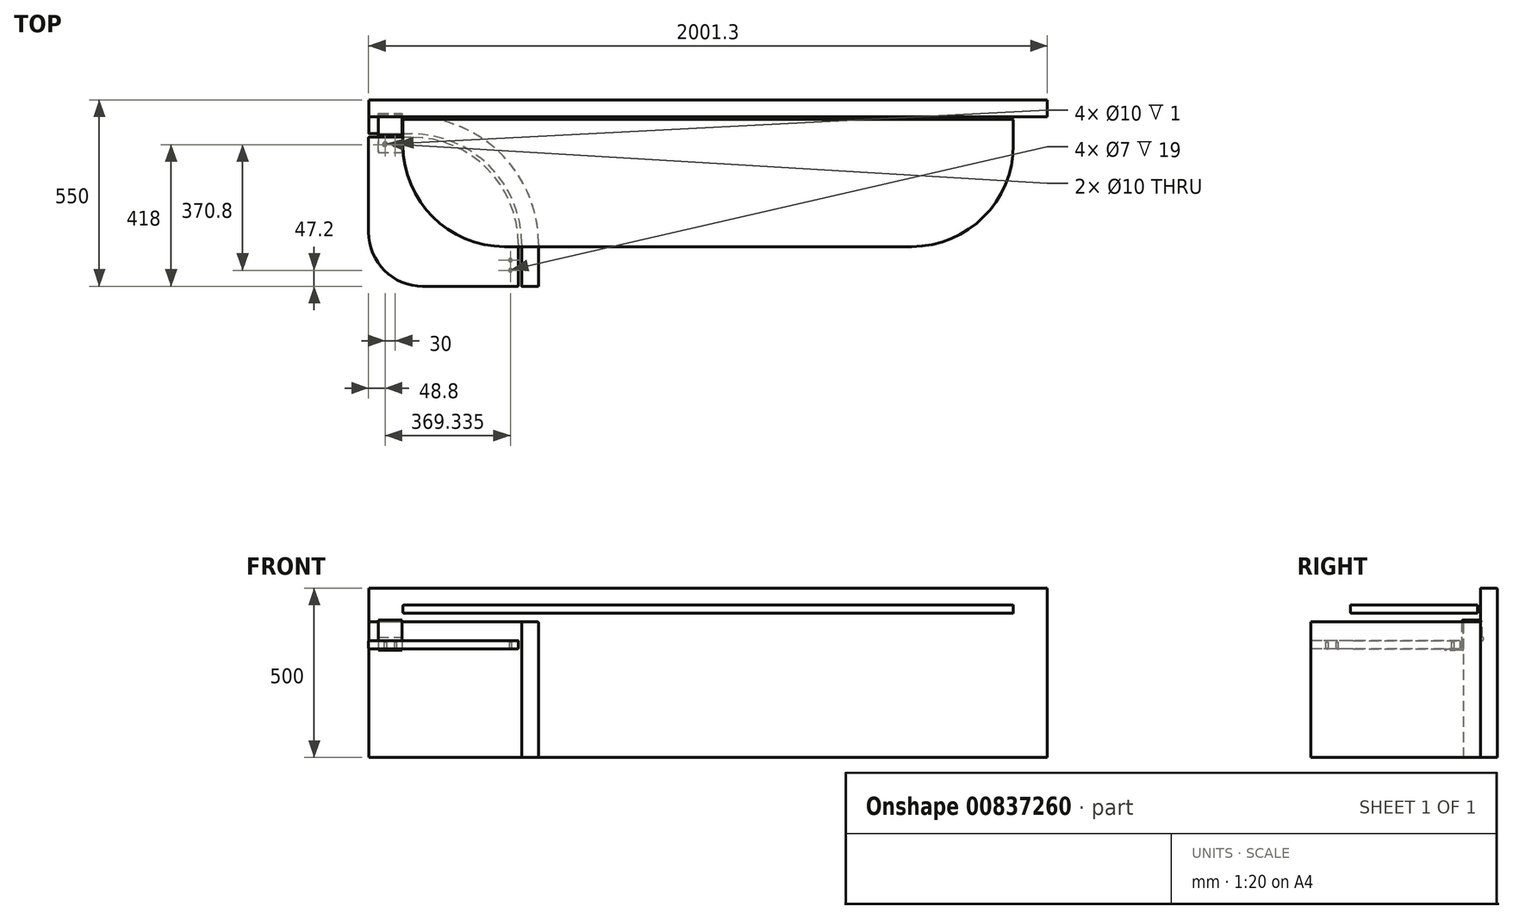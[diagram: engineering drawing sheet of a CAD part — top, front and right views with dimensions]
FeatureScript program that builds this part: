
annotation { "Feature Type Name" : "Feature", "Feature Type Description" : "" }
export const myFeature = defineFeature(function(context is Context, id is Id, definition is map)
    precondition{}
    {
        {
            var Q0;
            Q0=qCreatedBy(makeId("Top.planeOp"),FACE);
            var sketch = newSketch(context, id + "F0", { "sketchPlane" : qUnion([Q0])});
            skLineSegment(sketch, "E0.bottom", {"start": v(0, 0) * mm, "end": v(2000, 0) * mm});
            skLineSegment(sketch, "E0.top", {"start": v(0, 50) * mm, "end": v(2000, 50) * mm});
            skLineSegment(sketch, "E0.left", {"start": v(0, 0) * mm, "end": v(0, 50) * mm});
            skLineSegment(sketch, "E0.right", {"start": v(2000, 0) * mm, "end": v(2000, 50) * mm});
            skSolve(sketch);
        }
        {
            var Q0;
            Q0 = qSketchRegion(id + "F0", true);
            extrude(context, id + "F1", {"entities" : qUnion([Q0]), "depth" : 500 * mm, "offsetDistance" : 25 * mm});
        }
        {
            var Q0;
            Q0=makeQuery(id+"F1.opExtrude","CAP_FACE",FACE,{"disambiguationData":[OSD([sQuery(id+"F0.wireOp",EDGE,"E0.bottom"),sQuery(id+"F0.wireOp",EDGE,"E0.top"),sQuery(id+"F0.wireOp",EDGE,"E0.left"),sQuery(id+"F0.wireOp",EDGE,"E0.right")])],"isStart":false});
            cPlane(context, id + "F2", {"entities" : qUnion([Q0]), "cplaneType" : CPlaneType.OFFSET, "offset" : 74 * mm, "oppositeDirection" : true, "width" : 150 * mm, "height" : 150 * mm});
        }
        {
            var Q0;
            Q0=qCreatedBy(id+"F2.planeOp",FACE);
            var sketch = newSketch(context, id + "F3", { "sketchPlane" : qUnion([Q0])});
            skLineSegment(sketch, "E1.bottom", {"start": v(100, -8) * mm, "end": v(1900, -8) * mm});
            skLineSegment(sketch, "E1.top", {"start": v(400, -383) * mm, "end": v(1600, -383) * mm});
            skLineSegment(sketch, "E1.left", {"start": v(100, -8) * mm, "end": v(100, -83) * mm});
            skLineSegment(sketch, "E1.right", {"start": v(1900, -8) * mm, "end": v(1900, -83) * mm});
            skPoint(sketch, "E2.visualSharp", {"position": v(100, -383) * mm});
            skArc(sketch, "E2.filletArc", {"start": v(100, -83) * mm, "mid": v(187.87, -295.13) * mm, "end": v(400, -383) * mm});
            skPoint(sketch, "E3.visualSharp", {"position": v(1900, -383) * mm});
            skArc(sketch, "E3.filletArc", {"start": v(1600, -383) * mm, "mid": v(1812.13, -295.13) * mm, "end": v(1900, -83) * mm});
            skSolve(sketch);
        }
        {
            var Q0;
            Q0=makeQuery(id+"F3.imprint","IMPRINT",FACE,{"disambiguationData":[TD([[makeQuery(id+"F3.imprint","IMPRINT",EDGE,{"derivedFrom":sQuery(id+"F3.wireOp",EDGE,"E1.bottom")}),-1.0]])]});
            extrude(context, id + "F4", {"entities" : qUnion([Q0]), "depth" : 24 * mm, "offsetDistance" : 25 * mm});
        }
        {
            var Q0;
            Q0=makeQuery(id+"F1.opExtrude","CAP_EDGE",EDGE,{"disambiguationData":[OSD([sQuery(id+"F0.wireOp",EDGE,"E0.bottom")])],"isStart":false});
            var Q1;
            Q1=makeQuery(id+"F1.opExtrude","CAP_EDGE",EDGE,{"disambiguationData":[OSD([sQuery(id+"F0.wireOp",EDGE,"E0.top")])],"isStart":false});
            fillet(context, id + "F5", {"entities" : qUnion([Q0, Q1]), "radius" : 3 * mm, "tangentPropagation" : true, "allowEdgeOverflow" : false});
        }
        {
            var Q0;
            Q0=makeQuery(id+"F4.opExtrude","CAP_EDGE",EDGE,{"disambiguationData":[OSD([sQuery(id+"F3.wireOp",EDGE,"E1.left")])],"isStart":false});
            var Q1;
            Q1=makeQuery(id+"F4.opExtrude","CAP_EDGE",EDGE,{"disambiguationData":[OSD([sQuery(id+"F3.wireOp",EDGE,"E2.filletArc")])],"isStart":false});
            var Q2;
            Q2=makeQuery(id+"F4.opExtrude","CAP_EDGE",EDGE,{"disambiguationData":[OSD([sQuery(id+"F3.wireOp",EDGE,"E1.top")])],"isStart":true});
            var Q3;
            Q3=makeQuery(id+"F4.opExtrude","SWEPT_EDGE",EDGE,{"disambiguationData":[OSD([sQuery(id+"F3.wireOp",EDGE,"E1.bottom"),sQuery(id+"F3.wireOp",EDGE,"E1.left")])]});
            var Q4;
            Q4=makeQuery(id+"F4.opExtrude","CAP_EDGE",EDGE,{"disambiguationData":[OSD([sQuery(id+"F3.wireOp",EDGE,"E1.bottom")])],"isStart":false});
            var Q5;
            Q5=makeQuery(id+"F4.opExtrude","CAP_EDGE",EDGE,{"disambiguationData":[OSD([sQuery(id+"F3.wireOp",EDGE,"E1.bottom")])],"isStart":true});
            var Q6;
            Q6=makeQuery(id+"F4.opExtrude","SWEPT_EDGE",EDGE,{"disambiguationData":[OSD([sQuery(id+"F3.wireOp",EDGE,"E1.bottom"),sQuery(id+"F3.wireOp",EDGE,"E1.right")])]});
            fillet(context, id + "F6", {"entities" : qUnion([Q0, Q1, Q2, Q3, Q4, Q5, Q6]), "radius" : 2 * mm, "tangentPropagation" : true, "allowEdgeOverflow" : false});
        }
        {
            var Q0;
            Q0=qCreatedBy(makeId("Top.planeOp"),FACE);
            var sketch = newSketch(context, id + "F7", { "sketchPlane" : qUnion([Q0])});
            skLineSegment(sketch, "E4.bottom", {"start": v(0, 0) * mm, "end": v(125, 0) * mm});
            skLineSegment(sketch, "E4.top", {"start": v(0, -50) * mm, "end": v(125, -50) * mm});
            skLineSegment(sketch, "E4.left", {"start": v(0, 0) * mm, "end": v(0, -50) * mm});
            skLineSegment(sketch, "E4.right", {"start": v(500, 0) * mm, "end": v(500, -50) * mm});
            skLineSegment(sketch, "E5.bottom", {"start": v(500, 0) * mm, "end": v(450, 0) * mm});
            skLineSegment(sketch, "E5.top", {"start": v(500, -500) * mm, "end": v(450, -500) * mm});
            skLineSegment(sketch, "E5.left", {"start": v(500, -375) * mm, "end": v(500, -500) * mm});
            skLineSegment(sketch, "E5.right", {"start": v(450, -375) * mm, "end": v(450, -500) * mm});
            skPoint(sketch, "E6.visualSharp", {"position": v(450, -50) * mm});
            skArc(sketch, "E6.filletArc", {"start": v(450, -52.2) * mm, "mid": v(449.36, -50.64) * mm, "end": v(447.8, -50) * mm});
            skArc(sketch, "E7.filletArc", {"start": v(450, -375) * mm, "mid": v(354.8, -145.2) * mm, "end": v(125, -50) * mm});
            skPoint(sketch, "E8.visualSharp", {"position": v(500, 0) * mm});
            skArc(sketch, "E8.filletArc", {"start": v(500, -375) * mm, "mid": v(390.17, -109.83) * mm, "end": v(125, 0) * mm});
            skSolve(sketch);
        }
        {
            var Q0;
            Q0=makeQuery(id+"F7.imprint","IMPRINT",FACE,{"disambiguationData":[TD([[makeQuery(id+"F7.imprint","IMPRINT",EDGE,{"derivedFrom":sQuery(id+"F7.wireOp",EDGE,"E4.bottom")}),-1.0]])]});
            extrude(context, id + "F8", {"entities" : qUnion([Q0]), "depth" : 400 * mm, "offsetDistance" : 25 * mm});
        }
        {
            var Q0;
            Q0=makeQuery(id+"F8.opExtrude","SWEPT_FACE",FACE,{"disambiguationData":[OSD([sQuery(id+"F7.wireOp",EDGE,"E4.left")])]});
            cPlane(context, id + "F9", {"entities" : qUnion([Q0]), "cplaneType" : CPlaneType.OFFSET, "offset" : 62.5 * mm, "oppositeDirection" : true, "width" : 150 * mm, "height" : 150 * mm});
        }
        {
            var Q0;
            Q0=qCreatedBy(id+"F9.planeOp",FACE);
            var sketch = newSketch(context, id + "F10", { "sketchPlane" : qUnion([Q0])});
            skLineSegment(sketch, "E9", {"start": v(53, 316) * mm, "end": v(104, 316) * mm});
            skLineSegment(sketch, "E10", {"start": v(50, 319) * mm, "end": v(50, 397) * mm});
            skLineSegment(sketch, "E11", {"start": v(3, 400) * mm, "end": v(47, 400) * mm});
            skLineSegment(sketch, "E12", {"start": v(0, 397) * mm, "end": v(0, 350) * mm});
            skLineSegment(sketch, "E13", {"start": v(-5, 345) * mm, "end": v(-5, 402) * mm});
            skLineSegment(sketch, "E14", {"start": v(52, 405) * mm, "end": v(-2, 405) * mm});
            skLineSegment(sketch, "E15", {"start": v(55, 402) * mm, "end": v(55, 324) * mm});
            skLineSegment(sketch, "E16", {"start": v(104, 321) * mm, "end": v(58, 321) * mm});
            skCircle(sketch, "E17", {"center": v(-5, 350) * mm, "radius": 5 * mm});
            skLineSegment(sketch, "E18", {"start": v(105, 317) * mm, "end": v(105, 320) * mm});
            skPoint(sketch, "E19.visualSharp", {"position": v(0, 400) * mm});
            skArc(sketch, "E19.filletArc", {"start": v(3, 400) * mm, "mid": v(0.88, 399.12) * mm, "end": v(0, 397) * mm});
            skPoint(sketch, "E20.visualSharp", {"position": v(-5, 405) * mm});
            skArc(sketch, "E20.filletArc", {"start": v(-2, 405) * mm, "mid": v(-4.12, 404.12) * mm, "end": v(-5, 402) * mm});
            skPoint(sketch, "E21.visualSharp", {"position": v(55, 405) * mm});
            skArc(sketch, "E21.filletArc", {"start": v(55, 402) * mm, "mid": v(54.12, 404.12) * mm, "end": v(52, 405) * mm});
            skPoint(sketch, "E22.visualSharp", {"position": v(50, 400) * mm});
            skArc(sketch, "E22.filletArc", {"start": v(50, 397) * mm, "mid": v(49.12, 399.12) * mm, "end": v(47, 400) * mm});
            skPoint(sketch, "E23.visualSharp", {"position": v(50, 316) * mm});
            skArc(sketch, "E23.filletArc", {"start": v(50, 319) * mm, "mid": v(50.88, 316.88) * mm, "end": v(53, 316) * mm});
            skPoint(sketch, "E24.visualSharp", {"position": v(55, 321) * mm});
            skArc(sketch, "E24.filletArc", {"start": v(55, 324) * mm, "mid": v(55.88, 321.88) * mm, "end": v(58, 321) * mm});
            skPoint(sketch, "E25.visualSharp", {"position": v(105, 316) * mm});
            skArc(sketch, "E25.filletArc", {"start": v(104, 316) * mm, "mid": v(104.7, 316.3) * mm, "end": v(105, 317) * mm});
            skPoint(sketch, "E26.visualSharp", {"position": v(105, 321) * mm});
            skArc(sketch, "E26.filletArc", {"start": v(105, 320) * mm, "mid": v(104.7, 320.7) * mm, "end": v(104, 321) * mm});
            skSolve(sketch);
        }
        {
            var Q0;
            Q0 = qSketchRegion(id + "F10", true);
            extrude(context, id + "F11", {"entities" : qUnion([Q0]), "endBound" : BoundingType.SYMMETRIC, "depth" : 70 * mm, "offsetDistance" : 25 * mm});
        }
        {
            var Q0;
            Q0=makeQuery(id+"F11.opExtrude","SWEPT_FACE",FACE,{"disambiguationData":[OSD([sQuery(id+"F10.wireOp",EDGE,"E16")])]});
            var sketch = newSketch(context, id + "F12", { "sketchPlane" : qUnion([Q0])});
            skLineSegment(sketch, "E27.0", {"start": v(-1.3, -60) * mm, "end": v(125, -60) * mm});
            skArc(sketch, "E27.1", {"start": v(440, -375) * mm, "mid": v(347.74, -152.26) * mm, "end": v(125, -60) * mm});
            skLineSegment(sketch, "E27.2", {"start": v(440, -375) * mm, "end": v(440, -500) * mm});
            skLineSegment(sketch, "E28", {"start": v(-1.3, -60) * mm, "end": v(-1.3, -340) * mm});
            skLineSegment(sketch, "E29", {"start": v(158.7, -500) * mm, "end": v(440, -500) * mm});
            skPoint(sketch, "E30.visualSharp", {"position": v(-1.3, -500) * mm});
            skArc(sketch, "E30.filletArc", {"start": v(-1.3, -340) * mm, "mid": v(45.56, -453.14) * mm, "end": v(158.7, -500) * mm});
            skSolve(sketch);
        }
        {
            var Q0;
            Q0 = qSketchRegion(id + "F12", true);
            extrude(context, id + "F13", {"entities" : qUnion([Q0]), "depth" : 24 * mm, "offsetDistance" : 25 * mm});
        }
        {
            var Q0;
            Q0=makeQuery(id+"F11.opExtrude","SWEPT_FACE",FACE,{"disambiguationData":[OSD([sQuery(id+"F10.wireOp",EDGE,"E9")])]});
            var sketch = newSketch(context, id + "F14", { "sketchPlane" : qUnion([Q0])});
            skLineSegment(sketch, "E31", {"start": v(27.5, 53) * mm, "end": v(47.5, 53) * mm, "construction": true});
            skLineSegment(sketch, "E32", {"start": v(47.5, 53) * mm, "end": v(77.5, 53) * mm, "construction": true});
            skLineSegment(sketch, "E33", {"start": v(77.5, 53) * mm, "end": v(97.5, 53) * mm, "construction": true});
            skLineSegment(sketch, "E34", {"start": v(77.5, 104) * mm, "end": v(77.5, 53) * mm, "construction": true});
            skLineSegment(sketch, "E35", {"start": v(47.5, 104) * mm, "end": v(47.5, 53) * mm, "construction": true});
            skLineSegment(sketch, "E36", {"start": v(27.5, 82) * mm, "end": v(97.5, 82) * mm, "construction": true});
            skCircle(sketch, "E37", {"center": v(47.5, 82) * mm, "radius": 7.5 * mm});
            skLineSegment(sketch, "E38", {"start": v(62.5, 53) * mm, "end": v(62.5, 82) * mm, "construction": true});
            skCircle(sketch, "E39.MirrorC", {"center": v(77.5, 82) * mm, "radius": 7.5 * mm});
            skSolve(sketch);
        }
        {
            var Q0;
            Q0 = qSketchRegion(id + "F14", true);
            extrude(context, id + "F15", {"entities" : qUnion([Q0]), "operationType" : NewBodyOperationType.REMOVE, "oppositeDirection" : true, "depth" : 10 * mm, "offsetDistance" : 25 * mm, "hasDraft" : true, "draftAngle" : 45 * degree, "draftPullDirection" : true});
        }
        {
            var Q0;
            Q0=makeQuery(id+"F11.opExtrude","SWEPT_FACE",FACE,{"disambiguationData":[OSD([sQuery(id+"F10.wireOp",EDGE,"E9")])]});
            var sketch = newSketch(context, id + "F16", { "sketchPlane" : qUnion([Q0])});
            skCircle(sketch, "E40", {"center": v(47.5, 82) * mm, "radius": 5 * mm});
            skLineSegment(sketch, "E41", {"start": v(62.5, 105) * mm, "end": v(62.5, 50) * mm, "construction": true});
            skCircle(sketch, "E42.MirrorC", {"center": v(77.5, 82) * mm, "radius": 5 * mm});
            skLineSegment(sketch, "E43", {"start": v(347.74, 152.26) * mm, "end": v(45.56, 453.14) * mm, "construction": true});
            skCircle(sketch, "E44.MirrorC", {"center": v(416.84, 422.8) * mm, "radius": 5 * mm});
            skCircle(sketch, "E45.MirrorC", {"center": v(416.7, 452.8) * mm, "radius": 5 * mm});
            skSolve(sketch);
        }
        {
            var Q0;
            Q0 = qSketchRegion(id + "F16", true);
            extrude(context, id + "F17", {"entities" : qUnion([Q0]), "operationType" : NewBodyOperationType.REMOVE, "oppositeDirection" : true, "depth" : 6 * mm, "offsetDistance" : 25 * mm});
        }
        {
            var Q0;
            Q0=makeQuery(id+"F11.opExtrude","SWEPT_FACE",FACE,{"disambiguationData":[OSD([sQuery(id+"F10.wireOp",EDGE,"E9")])]});
            var sketch = newSketch(context, id + "F18", { "sketchPlane" : qUnion([Q0])});
            skCircle(sketch, "E46", {"center": v(47.5, 82) * mm, "radius": 3.5 * mm});
            skCircle(sketch, "E47", {"center": v(77.5, 82) * mm, "radius": 3.5 * mm});
            skLineSegment(sketch, "E48", {"start": v(347.74, 152.26) * mm, "end": v(45.56, 453.14) * mm, "construction": true});
            skCircle(sketch, "E49.MirrorC", {"center": v(416.84, 422.8) * mm, "radius": 3.5 * mm});
            skCircle(sketch, "E50.MirrorC", {"center": v(416.7, 452.8) * mm, "radius": 3.5 * mm});
            skSolve(sketch);
        }
        {
            var Q0;
            Q0 = qSketchRegion(id + "F18", true);
            extrude(context, id + "F19", {"entities" : qUnion([Q0]), "operationType" : NewBodyOperationType.REMOVE, "oppositeDirection" : true, "depth" : 25 * mm, "offsetDistance" : 25 * mm});
        }
        {
            var Q0;
            Q0=makeQuery(id+"F8.opExtrude","CAP_EDGE",EDGE,{"disambiguationData":[OSD([sQuery(id+"F7.wireOp",EDGE,"E7.filletArc")])],"isStart":false});
            var Q1;
            Q1=makeQuery(id+"F8.opExtrude","CAP_EDGE",EDGE,{"disambiguationData":[OSD([sQuery(id+"F7.wireOp",EDGE,"E4.bottom")])],"isStart":false});
            fillet(context, id + "F20", {"entities" : qUnion([Q0, Q1]), "radius" : 3 * mm, "tangentPropagation" : true, "allowEdgeOverflow" : false});
        }
        {
            var Q0;
            Q0=makeQuery(id+"F13.opExtrude","CAP_EDGE",EDGE,{"disambiguationData":[OSD([sQuery(id+"F12.wireOp",EDGE,"E28")])],"isStart":false});
            var Q1;
            Q1=makeQuery(id+"F13.opExtrude","CAP_EDGE",EDGE,{"disambiguationData":[OSD([sQuery(id+"F12.wireOp",EDGE,"E28")])],"isStart":true});
            var Q2;
            Q2=makeQuery(id+"F13.opExtrude","SWEPT_EDGE",EDGE,{"disambiguationData":[OSD([sQuery(id+"F12.wireOp",EDGE,"E27.0"),sQuery(id+"F12.wireOp",EDGE,"E28")])]});
            var Q3;
            Q3=makeQuery(id+"F13.opExtrude","CAP_EDGE",EDGE,{"disambiguationData":[OSD([sQuery(id+"F12.wireOp",EDGE,"E27.0")])],"isStart":false});
            var Q4;
            Q4=makeQuery(id+"F13.opExtrude","CAP_EDGE",EDGE,{"disambiguationData":[OSD([sQuery(id+"F12.wireOp",EDGE,"E27.0")])],"isStart":true});
            var Q5;
            Q5=makeQuery(id+"F13.opExtrude","SWEPT_EDGE",EDGE,{"disambiguationData":[OSD([sQuery(id+"F12.wireOp",EDGE,"E27.2"),sQuery(id+"F12.wireOp",EDGE,"E29")])]});
            fillet(context, id + "F21", {"entities" : qUnion([Q0, Q1, Q2, Q3, Q4, Q5]), "radius" : 2 * mm, "tangentPropagation" : true, "allowEdgeOverflow" : false});
        }
    });
